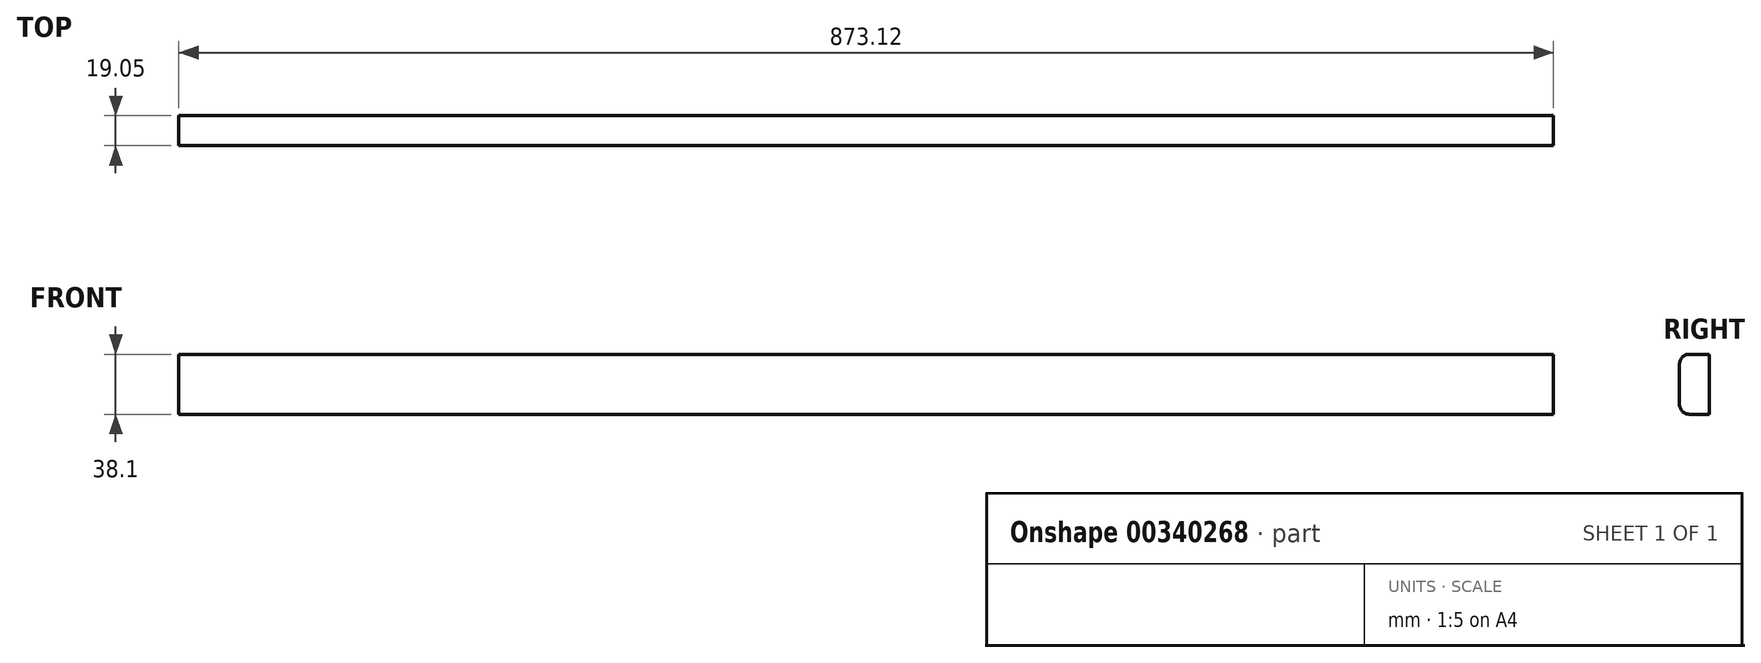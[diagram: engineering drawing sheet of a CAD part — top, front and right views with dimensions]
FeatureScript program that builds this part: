
annotation { "Feature Type Name" : "Feature", "Feature Type Description" : "" }
export const myFeature = defineFeature(function(context is Context, id is Id, definition is map)
    precondition{}
    {
        {
            var Q0;
            Q0=qCreatedBy(makeId("Front.planeOp"),FACE);
            var sketch = newSketch(context, id + "F0", { "sketchPlane" : qUnion([Q0])});
            skLineSegment(sketch, "E0.bottom", {"start": v(436.56, -19.05) * mm, "end": v(-436.56, -19.05) * mm});
            skLineSegment(sketch, "E0.top", {"start": v(436.56, 19.05) * mm, "end": v(-436.56, 19.05) * mm});
            skLineSegment(sketch, "E0.left", {"start": v(436.56, -19.05) * mm, "end": v(436.56, 19.05) * mm});
            skLineSegment(sketch, "E0.right", {"start": v(-436.56, -19.05) * mm, "end": v(-436.56, 19.05) * mm});
            skPoint(sketch, "E0.middle", {"position": v(0, 0) * mm});
            skSolve(sketch);
        }
        {
            var Q0;
            Q0 = qSketchRegion(id + "F0", true);
            extrude(context, id + "F1", {"entities" : qUnion([Q0]), "depth" : 19.05 * mm});
        }
        {
            var Q0;
            Q0=makeQuery(id+"F1.opExtrude","CAP_EDGE",EDGE,{"disambiguationData":[OSD([sQuery(id+"F0.wireOp",EDGE,"E0.top")])],"isStart":false});
            var Q1;
            Q1=makeQuery(id+"F1.opExtrude","CAP_EDGE",EDGE,{"disambiguationData":[OSD([sQuery(id+"F0.wireOp",EDGE,"E0.bottom")])],"isStart":false});
            fillet(context, id + "F2", {"entities" : qUnion([Q0, Q1]), "radius" : 6.35 * mm, "tangentPropagation" : true, "allowEdgeOverflow" : false});
        }
    });
